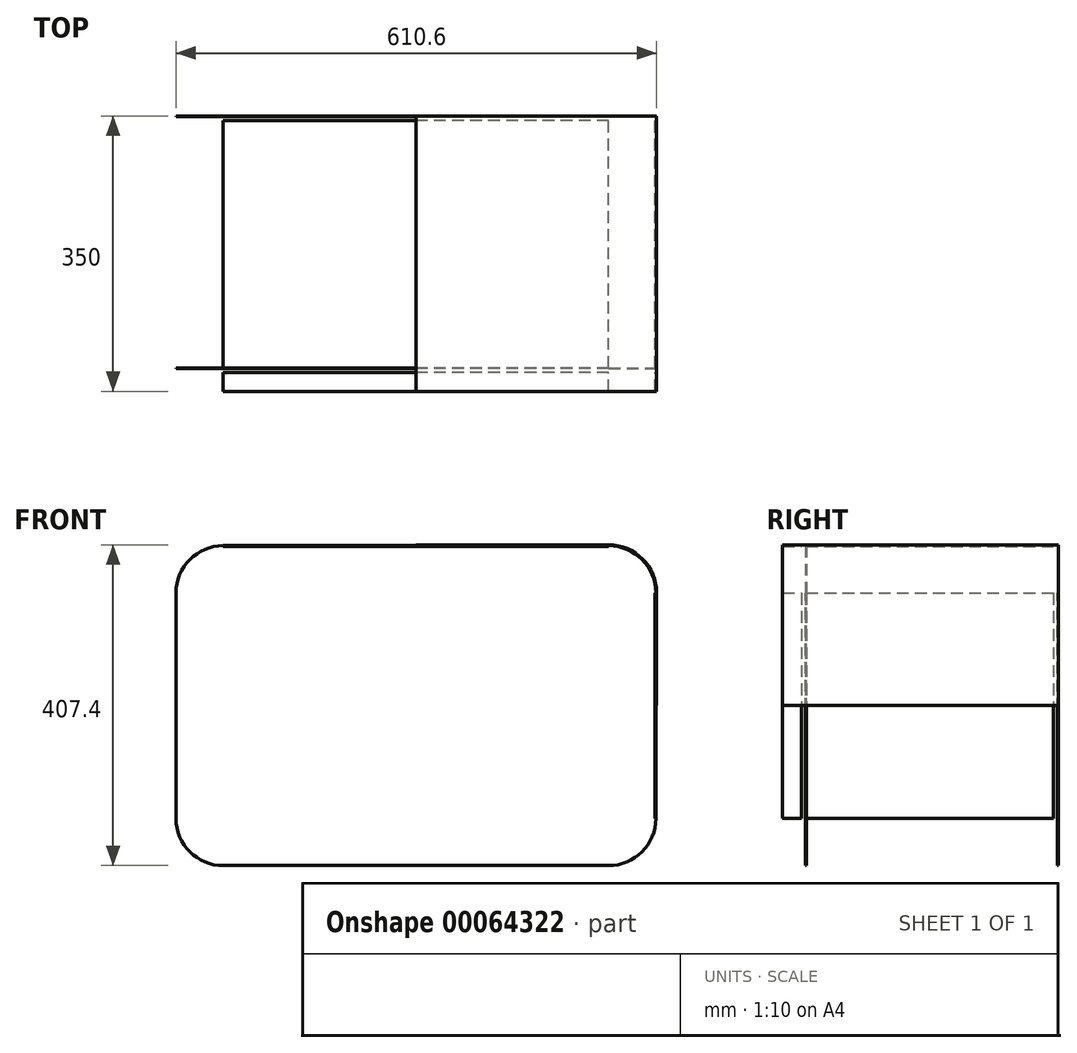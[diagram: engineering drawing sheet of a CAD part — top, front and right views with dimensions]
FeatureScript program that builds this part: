
annotation { "Feature Type Name" : "Feature", "Feature Type Description" : "" }
export const myFeature = defineFeature(function(context is Context, id is Id, definition is map)
    precondition{}
    {
        {
            assignVariable(context, id + "F0", {"name" : "m_thick", "anyValue" : 1 * mm});
        }
        {
            var Q0;
            Q0=qCreatedBy(makeId("Front.planeOp"),FACE);
            var sketch = newSketch(context, id + "F1", { "sketchPlane" : qUnion([Q0])});
            skLineSegment(sketch, "E0.rect.bottom", {"start": v(244.8, 203.2) * mm, "end": v(0, 203.2) * mm});
            skLineSegment(sketch, "E0.rect.left", {"start": v(304.8, 143.2) * mm, "end": v(304.8, 0) * mm});
            skPoint(sketch, "E0.rect.middle", {"position": v(0, 0) * mm});
            skPoint(sketch, "E1.visualSharp", {"position": v(304.8, 203.2) * mm});
            skArc(sketch, "E1.filletArc", {"start": v(304.8, 143.2) * mm, "mid": v(287.23, 185.63) * mm, "end": v(244.8, 203.2) * mm});
            skLineSegment(sketch, "E2", {"start": v(0, 0) * mm, "end": v(0, 526.98) * mm});
            skLineSegment(sketch, "E3", {"start": v(667.96, 0) * mm, "end": v(0, 0) * mm});
            skLineSegment(sketch, "E4.0", {"start": v(244.8, 204.2) * mm, "end": v(0, 204.2) * mm});
            skArc(sketch, "E4.1", {"start": v(305.8, 143.2) * mm, "mid": v(287.93, 186.33) * mm, "end": v(244.8, 204.2) * mm});
            skLineSegment(sketch, "E4.2", {"start": v(305.8, 143.2) * mm, "end": v(305.8, 0) * mm});
            skLineSegment(sketch, "E5.0", {"start": v(244.8, 202.2) * mm, "end": v(0, 202.2) * mm});
            skLineSegment(sketch, "E6.0", {"start": v(303.8, 143.2) * mm, "end": v(303.8, 0) * mm});
            skLineSegment(sketch, "E7.bottom", {"start": v(1425.63, 785.2) * mm, "end": v(3864.03, 785.2) * mm});
            skLineSegment(sketch, "E7.top", {"start": v(1425.63, -434) * mm, "end": v(3864.03, -434) * mm});
            skLineSegment(sketch, "E7.left", {"start": v(1425.63, 785.2) * mm, "end": v(1425.63, -434) * mm});
            skLineSegment(sketch, "E7.right", {"start": v(3864.03, 785.2) * mm, "end": v(3864.03, -434) * mm});
            skLineSegment(sketch, "E8.bottom", {"start": v(1421.93, -434) * mm, "end": v(2621.93, -434) * mm});
            skLineSegment(sketch, "E8.top", {"start": v(1421.93, 366) * mm, "end": v(2621.93, 366) * mm});
            skLineSegment(sketch, "E8.left", {"start": v(1421.93, -434) * mm, "end": v(1421.93, 366) * mm});
            skLineSegment(sketch, "E8.right", {"start": v(2621.93, -434) * mm, "end": v(2621.93, 366) * mm});
            skLineSegment(sketch, "E9", {"start": v(2644.83, -434) * mm, "end": v(2644.83, 785.2) * mm});
            skLineSegment(sketch, "E10.MirrorCS", {"start": v(-667.96, 0) * mm, "end": v(0, 0) * mm, "construction": true});
            skLineSegment(sketch, "E11", {"start": v(244.8, 202.2) * mm, "end": v(244.8, 203.2) * mm});
            skLineSegment(sketch, "E12", {"start": v(303.8, 143.2) * mm, "end": v(304.8, 143.2) * mm});
            skLineSegment(sketch, "E13.bottom", {"start": v(1396.97, -1773.98) * mm, "end": v(1746.97, -1773.98) * mm});
            skLineSegment(sketch, "E13.top", {"start": v(1396.97, -2518.98) * mm, "end": v(1746.97, -2518.98) * mm});
            skLineSegment(sketch, "E13.left", {"start": v(1396.97, -1773.98) * mm, "end": v(1396.97, -2518.98) * mm});
            skLineSegment(sketch, "E13.right", {"start": v(1746.97, -1773.98) * mm, "end": v(1746.97, -2518.98) * mm});
            skLineSegment(sketch, "E14.1.0.0", {"start": v(1746.97, -2518.98) * mm, "end": v(2096.97, -2518.98) * mm});
            skLineSegment(sketch, "E14.1.0.1", {"start": v(2096.97, -1773.98) * mm, "end": v(2096.97, -2518.98) * mm});
            skLineSegment(sketch, "E14.1.0.2", {"start": v(1746.97, -1773.98) * mm, "end": v(2096.97, -1773.98) * mm});
            skLineSegment(sketch, "E14.2.0.0", {"start": v(2096.97, -2518.98) * mm, "end": v(2446.97, -2518.98) * mm});
            skLineSegment(sketch, "E14.2.0.1", {"start": v(2446.97, -1773.98) * mm, "end": v(2446.97, -2518.98) * mm});
            skLineSegment(sketch, "E14.2.0.2", {"start": v(2096.97, -1773.98) * mm, "end": v(2446.97, -1773.98) * mm});
            skLineSegment(sketch, "E14.direction1", {"start": v(1396.97, -2518.98) * mm, "end": v(1746.97, -2518.98) * mm, "construction": true});
            skLineSegment(sketch, "E15.bottom", {"start": v(2698.8, -1773.27) * mm, "end": v(3048.8, -1773.27) * mm});
            skLineSegment(sketch, "E15.top", {"start": v(2698.8, -2518.27) * mm, "end": v(3048.8, -2518.27) * mm});
            skLineSegment(sketch, "E15.left", {"start": v(2698.8, -1773.27) * mm, "end": v(2698.8, -2518.27) * mm});
            skLineSegment(sketch, "E15.right", {"start": v(3048.8, -1773.27) * mm, "end": v(3048.8, -2518.27) * mm});
            skLineSegment(sketch, "E16.bottom", {"start": v(1430.76, -3016.82) * mm, "end": v(2225.76, -3016.82) * mm});
            skLineSegment(sketch, "E16.top", {"start": v(1430.76, -3316.82) * mm, "end": v(2225.76, -3316.82) * mm});
            skLineSegment(sketch, "E16.left", {"start": v(1430.76, -3016.82) * mm, "end": v(1430.76, -3316.82) * mm});
            skLineSegment(sketch, "E16.right", {"start": v(2225.76, -3016.82) * mm, "end": v(2225.76, -3316.82) * mm});
            skLineSegment(sketch, "E17.bottom", {"start": v(4728.96, 341) * mm, "end": v(5643.36, 341) * mm});
            skLineSegment(sketch, "E17.top", {"start": v(4728.96, -268.6) * mm, "end": v(5643.36, -268.6) * mm});
            skLineSegment(sketch, "E17.left", {"start": v(4728.96, 341) * mm, "end": v(4728.96, -268.6) * mm});
            skLineSegment(sketch, "E17.right", {"start": v(5643.36, 341) * mm, "end": v(5643.36, -268.6) * mm});
            skLineSegment(sketch, "E18.bottom", {"start": v(3200.39, -380.36) * mm, "end": v(3809.99, -380.36) * mm});
            skLineSegment(sketch, "E18.top", {"start": v(3200.39, 534.04) * mm, "end": v(3809.99, 534.04) * mm});
            skLineSegment(sketch, "E18.left", {"start": v(3200.39, -380.36) * mm, "end": v(3200.39, 534.04) * mm});
            skLineSegment(sketch, "E18.right", {"start": v(3809.99, -380.36) * mm, "end": v(3809.99, 534.04) * mm});
            skLineSegment(sketch, "E19.bottom", {"start": v(3993.98, -1809.5) * mm, "end": v(6433.98, -1809.5) * mm});
            skLineSegment(sketch, "E19.top", {"start": v(3993.98, -3029.5) * mm, "end": v(6433.98, -3029.5) * mm});
            skLineSegment(sketch, "E19.left", {"start": v(3993.98, -1809.5) * mm, "end": v(3993.98, -3029.5) * mm});
            skLineSegment(sketch, "E19.right", {"start": v(6433.98, -1809.5) * mm, "end": v(6433.98, -3029.5) * mm});
            skLineSegment(sketch, "E20", {"start": v(5213.98, -1809.5) * mm, "end": v(5213.98, -3029.5) * mm});
            skLineSegment(sketch, "E21", {"start": v(3993.98, -2229.5) * mm, "end": v(5213.98, -2229.5) * mm});
            skLineSegment(sketch, "E22", {"start": v(5773.98, -1809.5) * mm, "end": v(5773.98, -3029.5) * mm});
            skLineSegment(sketch, "E23.MirrorCS", {"start": v(-303.8, 143.2) * mm, "end": v(-304.8, 143.2) * mm});
            skLineSegment(sketch, "E24.MirrorCS", {"start": v(-244.8, 202.2) * mm, "end": v(-244.8, 203.2) * mm});
            skArc(sketch, "E25.MirrorCS", {"start": v(-304.8, 143.2) * mm, "mid": v(-287.23, 185.63) * mm, "end": v(-244.8, 203.2) * mm});
            skArc(sketch, "E26.MirrorCS", {"start": v(-305.8, 143.2) * mm, "mid": v(-287.93, 186.33) * mm, "end": v(-244.8, 204.2) * mm});
            skLineSegment(sketch, "E27.MirrorCS", {"start": v(-304.8, 143.2) * mm, "end": v(-304.8, 0) * mm});
            skLineSegment(sketch, "E28.MirrorCS", {"start": v(-244.8, 203.2) * mm, "end": v(0, 203.2) * mm});
            skPoint(sketch, "E29.MirrorP", {"position": v(-304.8, 203.2) * mm});
            skLineSegment(sketch, "E30.MirrorCS", {"start": v(-303.8, 143.2) * mm, "end": v(-303.8, 0) * mm});
            skLineSegment(sketch, "E31.MirrorCS", {"start": v(-244.8, 202.2) * mm, "end": v(0, 202.2) * mm});
            skLineSegment(sketch, "E32.MirrorCS", {"start": v(-244.8, 204.2) * mm, "end": v(0, 204.2) * mm});
            skLineSegment(sketch, "E33.MirrorCS", {"start": v(-305.8, 143.2) * mm, "end": v(-305.8, 0) * mm});
            skLineSegment(sketch, "E34.MirrorCS", {"start": v(303.8, -143.2) * mm, "end": v(304.8, -143.2) * mm});
            skLineSegment(sketch, "E35.MirrorCS", {"start": v(244.8, -202.2) * mm, "end": v(244.8, -203.2) * mm});
            skLineSegment(sketch, "E36.MirrorCS", {"start": v(244.8, -203.2) * mm, "end": v(0, -203.2) * mm});
            skLineSegment(sketch, "E37.MirrorCS", {"start": v(304.8, -143.2) * mm, "end": v(304.8, 0) * mm});
            skArc(sketch, "E38.MirrorCS", {"start": v(304.8, -143.2) * mm, "mid": v(287.23, -185.63) * mm, "end": v(244.8, -203.2) * mm});
            skLineSegment(sketch, "E39.MirrorCS", {"start": v(305.8, -143.2) * mm, "end": v(305.8, 0) * mm});
            skLineSegment(sketch, "E40.MirrorCS", {"start": v(244.8, -202.2) * mm, "end": v(0, -202.2) * mm});
            skLineSegment(sketch, "E41.MirrorCS", {"start": v(244.8, -204.2) * mm, "end": v(0, -204.2) * mm});
            skPoint(sketch, "E42.MirrorP", {"position": v(304.8, -203.2) * mm});
            skLineSegment(sketch, "E43.MirrorCS", {"start": v(303.8, -143.2) * mm, "end": v(303.8, 0) * mm});
            skArc(sketch, "E44.MirrorCS", {"start": v(305.8, -143.2) * mm, "mid": v(287.93, -186.33) * mm, "end": v(244.8, -204.2) * mm});
            skLineSegment(sketch, "E45.MirrorCS", {"start": v(-244.8, -202.2) * mm, "end": v(-244.8, -203.2) * mm});
            skLineSegment(sketch, "E46.MirrorCS", {"start": v(-303.8, -143.2) * mm, "end": v(-304.8, -143.2) * mm});
            skLineSegment(sketch, "E47.MirrorCS", {"start": v(-304.8, -143.2) * mm, "end": v(-304.8, 0) * mm});
            skLineSegment(sketch, "E48.MirrorCS", {"start": v(-244.8, -202.2) * mm, "end": v(0, -202.2) * mm});
            skArc(sketch, "E49.MirrorCS", {"start": v(-304.8, -143.2) * mm, "mid": v(-287.23, -185.63) * mm, "end": v(-244.8, -203.2) * mm});
            skLineSegment(sketch, "E50.MirrorCS", {"start": v(-305.8, -143.2) * mm, "end": v(-305.8, 0) * mm});
            skLineSegment(sketch, "E51.MirrorCS", {"start": v(-244.8, -204.2) * mm, "end": v(0, -204.2) * mm});
            skLineSegment(sketch, "E52.MirrorCS", {"start": v(-244.8, -203.2) * mm, "end": v(0, -203.2) * mm});
            skArc(sketch, "E53.MirrorCS", {"start": v(-305.8, -143.2) * mm, "mid": v(-287.93, -186.33) * mm, "end": v(-244.8, -204.2) * mm});
            skPoint(sketch, "E54.MirrorP", {"position": v(-304.8, -203.2) * mm});
            skLineSegment(sketch, "E55.MirrorCS", {"start": v(-303.8, -143.2) * mm, "end": v(-303.8, 0) * mm});
            skSolve(sketch);
        }
        {
            var Q0;
            {var subQ1=sQuery(id+"F1.wireOp",EDGE,"E0.rect.bottom");Q0=makeQuery(id+"F1.imprint","IMPRINT",FACE,{"disambiguationData":[TD([[makeQuery(id+"F1.imprint","IMPRINT",EDGE,{"derivedFrom":subQ1}),-1.0]])]});}
            extrude(context, id + "F2", {"entities" : qUnion([Q0]), "depth" : 350 * mm});
        }
        {
            var Q0;
            {var subQ0=sQuery(id+"F1.wireOp",EDGE,"e44dd1af-52c9-41d0-b528-caf0e91c3b952.MirrorCS");Q0=makeQuery(id+"F1.imprint","IMPRINT",FACE,{"disambiguationData":[TD([[makeQuery(id+"F1.imprint","IMPRINT",EDGE,{"derivedFrom":subQ0}),-1.0]])]});}
            var Q1;
            {var subQ0=sQuery(id+"F1.wireOp",EDGE,"E0.rect.bottom");Q1=makeQuery(id+"F1.imprint","IMPRINT",FACE,{"disambiguationData":[TD([[makeQuery(id+"F1.imprint","IMPRINT",EDGE,{"derivedFrom":subQ0}),1.0]])]});}
            var Q2;
            {var subQ0=sQuery(id+"F1.wireOp",EDGE,"E0.rect.left");Q2=makeQuery(id+"F1.imprint","IMPRINT",FACE,{"disambiguationData":[TD([[makeQuery(id+"F1.imprint","IMPRINT",EDGE,{"derivedFrom":subQ0}),-1.0]])]});}
            var Q3;
            {var subQ0=sQuery(id+"F1.wireOp",EDGE,"a96617ce-7221-4b49-972d-fbe93d66e1b02.MirrorCS");Q3=makeQuery(id+"F1.imprint","IMPRINT",FACE,{"disambiguationData":[TD([[makeQuery(id+"F1.imprint","IMPRINT",EDGE,{"derivedFrom":subQ0}),1.0]])]});}
            var Q4;
            Q4=makeQuery(id+"F1.imprint","IMPRINT",FACE,{"disambiguationData":[TD([[makeQuery(id+"F1.imprint","IMPRINT",EDGE,{"derivedFrom":sQuery(id+"F1.wireOp",EDGE,"E24.MirrorCS")}),-1.0]])]});
            var Q5;
            Q5=makeQuery(id+"F1.imprint","IMPRINT",FACE,{"disambiguationData":[TD([[makeQuery(id+"F1.imprint","IMPRINT",EDGE,{"derivedFrom":sQuery(id+"F1.wireOp",EDGE,"E34.MirrorCS")}),1.0]])]});
            extrude(context, id + "F3", {"entities" : qUnion([Q0, Q1, Q2, Q3, Q4, Q5]), "depth" : 314 * mm});
        }
        {
            var Q0;
            Q0=makeQuery(id+"F3.opExtrude","SWEPT_BODY",BODY,{"disambiguationData":[OSD([sQuery(id+"F1.wireOp",EDGE,"E0.rect.bottom"),sQuery(id+"F1.wireOp",EDGE,"E5.0"),sQuery(id+"F1.wireOp",EDGE,"e44dd1af-52c9-41d0-b528-caf0e91c3b952.MirrorCS"),sQuery(id+"F1.wireOp",EDGE,"e44dd1af-52c9-41d0-b528-caf0e91c3b9514.MirrorCS"),sQuery(id+"F1.wireOp",EDGE,"E11"),sQuery(id+"F1.wireOp",EDGE,"73b583ea-78f0-471c-b730-834146c9524e0.MirrorCS")])]});
            var Q1;
            Q1=makeQuery(id+"F3.opExtrude","SWEPT_BODY",BODY,{"disambiguationData":[OSD([sQuery(id+"F1.wireOp",EDGE,"E0.rect.left"),sQuery(id+"F1.wireOp",EDGE,"E6.0"),sQuery(id+"F1.wireOp",EDGE,"a96617ce-7221-4b49-972d-fbe93d66e1b02.MirrorCS"),sQuery(id+"F1.wireOp",EDGE,"a96617ce-7221-4b49-972d-fbe93d66e1b04.MirrorCS"),sQuery(id+"F1.wireOp",EDGE,"E12"),sQuery(id+"F1.wireOp",EDGE,"5690fcac-7ac8-4051-b4bb-74e52cf9e4670.MirrorCS")])]});
            var Q2;
            Q2=makeQuery(id+"F2.opExtrude","SWEPT_EDGE",EDGE,{"disambiguationData":[OSD([sQuery(id+"F1.wireOp",EDGE,"E3"),sQuery(id+"F1.wireOp",EDGE,"E4.2"),sQuery(id+"F1.wireOp",EDGE,"E39.MirrorCS")])]});
            transform(context, id + "F4", {"entities" : qUnion([Q0, Q1]), "transformType" : TransformType.TRANSLATION_DISTANCE, "transformDirection" : qUnion([Q2]), "distance" : 6 * mm, "oppositeDirection" : true, "makeCopy" : false});
        }
        {
            var Q0;
            {var subQ0=sQuery(id+"F1.wireOp",EDGE,"E0.rect.bottom");Q0=makeQuery(id+"F1.imprint","IMPRINT",FACE,{"disambiguationData":[TD([[makeQuery(id+"F1.imprint","IMPRINT",EDGE,{"derivedFrom":subQ0}),1.0]])]});}
            var Q1;
            {var subQ0=sQuery(id+"F1.wireOp",EDGE,"E0.rect.left");Q1=makeQuery(id+"F1.imprint","IMPRINT",FACE,{"disambiguationData":[TD([[makeQuery(id+"F1.imprint","IMPRINT",EDGE,{"derivedFrom":subQ0}),-1.0]])]});}
            var Q2;
            {var subQ0=sQuery(id+"F1.wireOp",EDGE,"e44dd1af-52c9-41d0-b528-caf0e91c3b952.MirrorCS");Q2=makeQuery(id+"F1.imprint","IMPRINT",FACE,{"disambiguationData":[TD([[makeQuery(id+"F1.imprint","IMPRINT",EDGE,{"derivedFrom":subQ0}),-1.0]])]});}
            var Q3;
            {var subQ0=sQuery(id+"F1.wireOp",EDGE,"a96617ce-7221-4b49-972d-fbe93d66e1b02.MirrorCS");Q3=makeQuery(id+"F1.imprint","IMPRINT",FACE,{"disambiguationData":[TD([[makeQuery(id+"F1.imprint","IMPRINT",EDGE,{"derivedFrom":subQ0}),1.0]])]});}
            var Q4;
            Q4=makeQuery(id+"F1.imprint","IMPRINT",FACE,{"disambiguationData":[TD([[makeQuery(id+"F1.imprint","IMPRINT",EDGE,{"derivedFrom":sQuery(id+"F1.wireOp",EDGE,"E24.MirrorCS")}),-1.0]])]});
            var Q5;
            Q5=makeQuery(id+"F1.imprint","IMPRINT",FACE,{"disambiguationData":[TD([[makeQuery(id+"F1.imprint","IMPRINT",EDGE,{"derivedFrom":sQuery(id+"F1.wireOp",EDGE,"E34.MirrorCS")}),1.0]])]});
            extrude(context, id + "F5", {"entities" : qUnion([Q0, Q1, Q2, Q3, Q4, Q5]), "depth" : 24 * mm});
        }
        {
            var Q0;
            Q0=makeQuery(id+"F5.opExtrude","SWEPT_BODY",BODY,{"disambiguationData":[OSD([sQuery(id+"F1.wireOp",EDGE,"E0.rect.left"),sQuery(id+"F1.wireOp",EDGE,"E6.0"),sQuery(id+"F1.wireOp",EDGE,"a96617ce-7221-4b49-972d-fbe93d66e1b02.MirrorCS"),sQuery(id+"F1.wireOp",EDGE,"a96617ce-7221-4b49-972d-fbe93d66e1b04.MirrorCS"),sQuery(id+"F1.wireOp",EDGE,"E12"),sQuery(id+"F1.wireOp",EDGE,"5690fcac-7ac8-4051-b4bb-74e52cf9e4670.MirrorCS")])]});
            var Q1;
            Q1=makeQuery(id+"F5.opExtrude","SWEPT_BODY",BODY,{"disambiguationData":[OSD([sQuery(id+"F1.wireOp",EDGE,"E0.rect.bottom"),sQuery(id+"F1.wireOp",EDGE,"E5.0"),sQuery(id+"F1.wireOp",EDGE,"e44dd1af-52c9-41d0-b528-caf0e91c3b952.MirrorCS"),sQuery(id+"F1.wireOp",EDGE,"e44dd1af-52c9-41d0-b528-caf0e91c3b9514.MirrorCS"),sQuery(id+"F1.wireOp",EDGE,"E11"),sQuery(id+"F1.wireOp",EDGE,"73b583ea-78f0-471c-b730-834146c9524e0.MirrorCS")])]});
            var Q2;
            Q2=makeQuery(id+"F3.opExtrude","SWEPT_EDGE",EDGE,{"disambiguationData":[OSD([sQuery(id+"F1.wireOp",EDGE,"E5.0"),sQuery(id+"F1.wireOp",EDGE,"E11")])]});
            transform(context, id + "F6", {"entities" : qUnion([Q0, Q1]), "transformType" : TransformType.TRANSLATION_DISTANCE, "transformDirection" : qUnion([Q2]), "distance" : 326 * mm, "oppositeDirection" : true, "makeCopy" : false});
        }
        {
            var Q0;
            {var subQ0=sQuery(id+"F1.wireOp",EDGE,"E0.rect.bottom");Q0=makeQuery(id+"F1.imprint","IMPRINT",FACE,{"disambiguationData":[TD([[makeQuery(id+"F1.imprint","IMPRINT",EDGE,{"derivedFrom":subQ0}),1.0]])]});}
            var Q1;
            Q1=makeQuery(id+"F1.imprint","IMPRINT",FACE,{"disambiguationData":[TD([[makeQuery(id+"F1.imprint","IMPRINT",EDGE,{"derivedFrom":sQuery(id+"F1.wireOp",EDGE,"E1.filletArc")}),1.0]])]});
            var Q2;
            {var subQ0=sQuery(id+"F1.wireOp",EDGE,"E0.rect.left");Q2=makeQuery(id+"F1.imprint","IMPRINT",FACE,{"disambiguationData":[TD([[makeQuery(id+"F1.imprint","IMPRINT",EDGE,{"derivedFrom":subQ0}),-1.0]])]});}
            var Q3;
            Q3=makeQuery(id+"F1.imprint","IMPRINT",FACE,{"disambiguationData":[TD([[makeQuery(id+"F1.imprint","IMPRINT",EDGE,{"derivedFrom":sQuery(id+"F1.wireOp",EDGE,"E24.MirrorCS")}),-1.0]])]});
            var Q4;
            Q4=makeQuery(id+"F1.imprint","IMPRINT",FACE,{"disambiguationData":[TD([[makeQuery(id+"F1.imprint","IMPRINT",EDGE,{"derivedFrom":sQuery(id+"F1.wireOp",EDGE,"E23.MirrorCS")}),1.0]])]});
            var Q5;
            Q5=makeQuery(id+"F1.imprint","IMPRINT",FACE,{"disambiguationData":[TD([[makeQuery(id+"F1.imprint","IMPRINT",EDGE,{"derivedFrom":sQuery(id+"F1.wireOp",EDGE,"E35.MirrorCS")}),-1.0]])]});
            var Q6;
            Q6=makeQuery(id+"F1.imprint","IMPRINT",FACE,{"disambiguationData":[TD([[makeQuery(id+"F1.imprint","IMPRINT",EDGE,{"derivedFrom":sQuery(id+"F1.wireOp",EDGE,"E34.MirrorCS")}),1.0]])]});
            var Q7;
            Q7=makeQuery(id+"F1.imprint","IMPRINT",FACE,{"disambiguationData":[TD([[makeQuery(id+"F1.imprint","IMPRINT",EDGE,{"derivedFrom":sQuery(id+"F1.wireOp",EDGE,"E23.MirrorCS")}),-1.0]])]});
            extrude(context, id + "F7", {"entities" : qUnion([Q0, Q1, Q2, Q3, Q4, Q5, Q6, Q7]), "depth" : getVariable(context, 'm_thick')});
        }
        {
            var Q0;
            Q0=makeQuery(id+"F7.opExtrude","SWEPT_BODY",BODY,{"disambiguationData":[OSD([sQuery(id+"F1.wireOp",EDGE,"E0.rect.bottom"),sQuery(id+"F1.wireOp",EDGE,"E0.rect.left"),sQuery(id+"F1.wireOp",EDGE,"E1.filletArc"),sQuery(id+"F1.wireOp",EDGE,"a96617ce-7221-4b49-972d-fbe93d66e1b01.MirrorCS"),sQuery(id+"F1.wireOp",EDGE,"a96617ce-7221-4b49-972d-fbe93d66e1b02.MirrorCS"),sQuery(id+"F1.wireOp",EDGE,"a96617ce-7221-4b49-972d-fbe93d66e1b05.MirrorCS"),sQuery(id+"F1.wireOp",EDGE,"e44dd1af-52c9-41d0-b528-caf0e91c3b951.MirrorCS"),sQuery(id+"F1.wireOp",EDGE,"e44dd1af-52c9-41d0-b528-caf0e91c3b952.MirrorCS"),sQuery(id+"F1.wireOp",EDGE,"e44dd1af-52c9-41d0-b528-caf0e91c3b953.MirrorCS"),sQuery(id+"F1.wireOp",EDGE,"e44dd1af-52c9-41d0-b528-caf0e91c3b955.MirrorCS"),sQuery(id+"F1.wireOp",EDGE,"e44dd1af-52c9-41d0-b528-caf0e91c3b957.MirrorCS"),sQuery(id+"F1.wireOp",EDGE,"e44dd1af-52c9-41d0-b528-caf0e91c3b9512.MirrorCS")])]});
            var Q1;
            Q1=makeQuery(id+"F3.opExtrude","SWEPT_EDGE",EDGE,{"disambiguationData":[OSD([sQuery(id+"F1.wireOp",EDGE,"a96617ce-7221-4b49-972d-fbe93d66e1b04.MirrorCS"),sQuery(id+"F1.wireOp",EDGE,"5690fcac-7ac8-4051-b4bb-74e52cf9e4670.MirrorCS")])]});
            var Q2;
            Q2=makeQuery(id+"F2.opExtrude","SWEPT_EDGE",EDGE,{"disambiguationData":[OSD([sQuery(id+"F1.wireOp",EDGE,"E3"),sQuery(id+"F1.wireOp",EDGE,"E4.2"),sQuery(id+"F1.wireOp",EDGE,"E39.MirrorCS")])]});
            transform(context, id + "F8", {"entities" : qUnion([Q0]), "transformType" : TransformType.TRANSLATION_DISTANCE, "transformDirection" : qUnion([Q2]), "distance" : 320 * mm, "oppositeDirection" : true, "makeCopy" : true});
        }
    });
